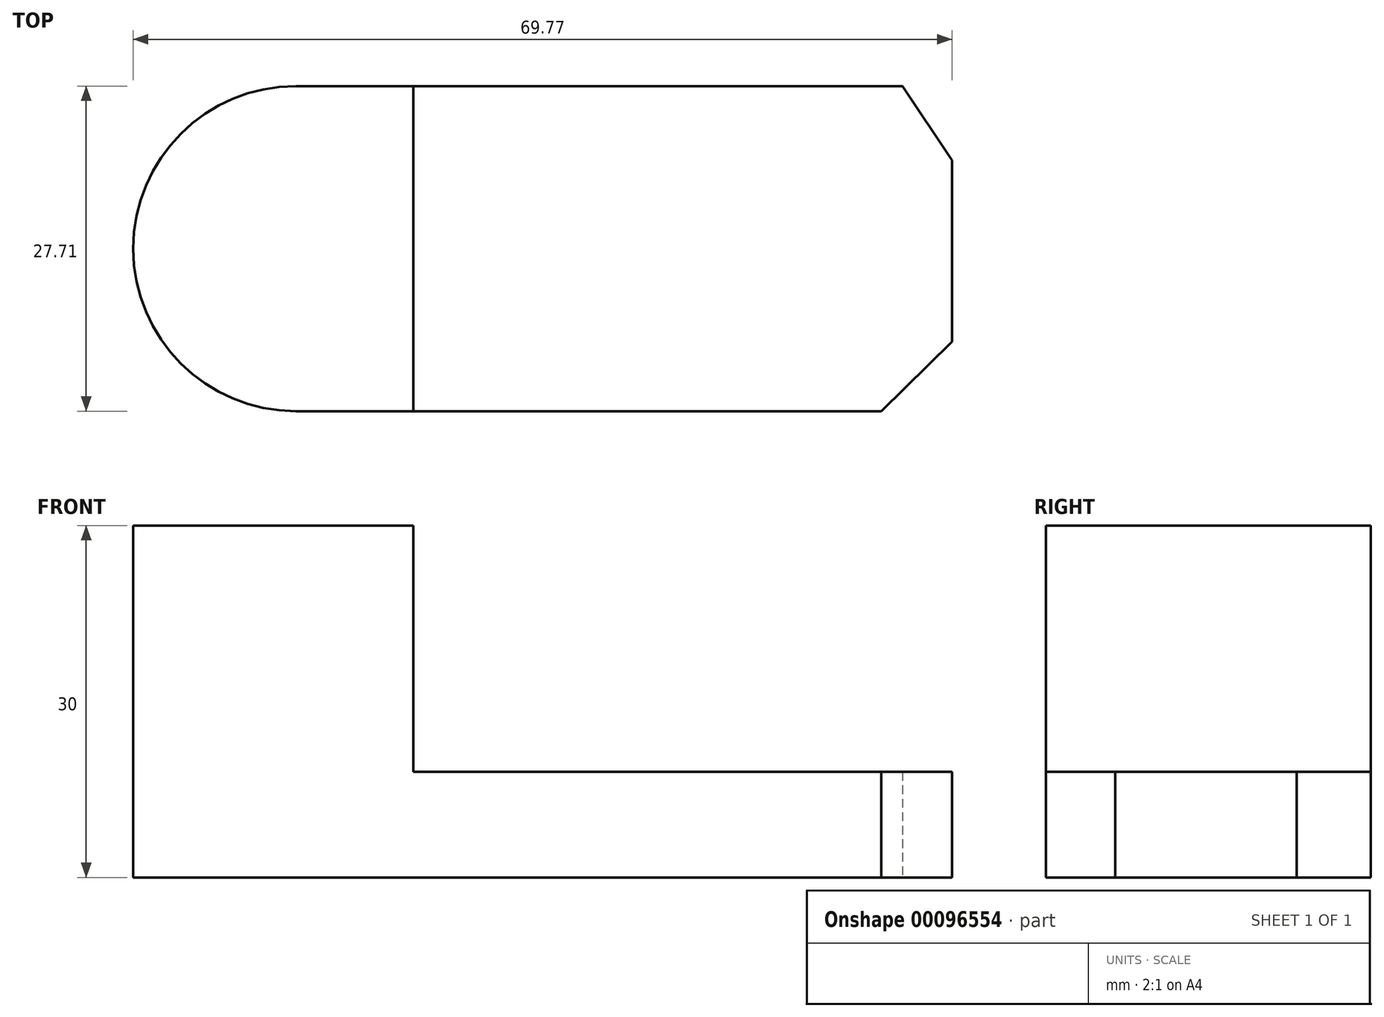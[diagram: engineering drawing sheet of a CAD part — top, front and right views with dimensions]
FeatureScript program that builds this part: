
annotation { "Feature Type Name" : "Feature", "Feature Type Description" : "" }
export const myFeature = defineFeature(function(context is Context, id is Id, definition is map)
    precondition{}
    {
        {
            var Q0;
            Q0=qCreatedBy(makeId("Top.planeOp"),FACE);
            var sketch = newSketch(context, id + "F0", { "sketchPlane" : qUnion([Q0])});
            skLineSegment(sketch, "E0.bottom", {"start": v(0, 0) * mm, "end": v(49.9, 0) * mm});
            skLineSegment(sketch, "E0.top", {"start": v(0, 27.71) * mm, "end": v(51.69, 27.71) * mm});
            skLineSegment(sketch, "E0.right", {"start": v(55.91, 5.93) * mm, "end": v(55.91, 21.37) * mm});
            skArc(sketch, "E1", {"start": v(0, 27.71) * mm, "mid": v(-13.86, 13.86) * mm, "end": v(0, 0) * mm});
            skLineSegment(sketch, "E2", {"start": v(51.69, 27.71) * mm, "end": v(55.91, 21.37) * mm});
            skLineSegment(sketch, "E3", {"start": v(55.91, 21.37) * mm, "end": v(55.91, 5.93) * mm});
            skLineSegment(sketch, "E4", {"start": v(55.91, 5.93) * mm, "end": v(49.9, 0) * mm});
            skSolve(sketch);
        }
        {
            var Q0;
            Q0=makeQuery(id+"F0.imprint","IMPRINT",FACE,{"disambiguationData":[TD([[makeQuery(id+"F0.imprint","IMPRINT",EDGE,{"derivedFrom":sQuery(id+"F0.wireOp",EDGE,"E0.bottom")}),1.0]])]});
            extrude(context, id + "F1", {"entities" : qUnion([Q0]), "depth" : 9 * mm});
        }
        {
            var Q0;
            Q0=makeQuery(id+"F1.opExtrude","CAP_FACE",FACE,{"disambiguationData":[OSD([sQuery(id+"F0.wireOp",EDGE,"E0.bottom"),sQuery(id+"F0.wireOp",EDGE,"E0.top"),sQuery(id+"F0.wireOp",EDGE,"E1"),sQuery(id+"F0.wireOp",EDGE,"E2"),sQuery(id+"F0.wireOp",EDGE,"E3"),sQuery(id+"F0.wireOp",EDGE,"E4")])],"isStart":false});
            var sketch = newSketch(context, id + "F2", { "sketchPlane" : qUnion([Q0])});
            skLineSegment(sketch, "E5", {"start": v(10, 27.71) * mm, "end": v(10, 0) * mm});
            skSolve(sketch);
        }
        {
            var Q0;
            {var subQ0=sQuery(id+"F2.wireOp",EDGE,"E5");Q0=makeQuery(id+"F2.imprint","IMPRINT",FACE,{"disambiguationData":[TD([[makeQuery(id+"F2.imprint","IMPRINT",EDGE,{"derivedFrom":subQ0}),-1.0]])]});}
            extrude(context, id + "F3", {"entities" : qUnion([Q0]), "operationType" : NewBodyOperationType.ADD, "depth" : 21 * mm});
        }
    });
